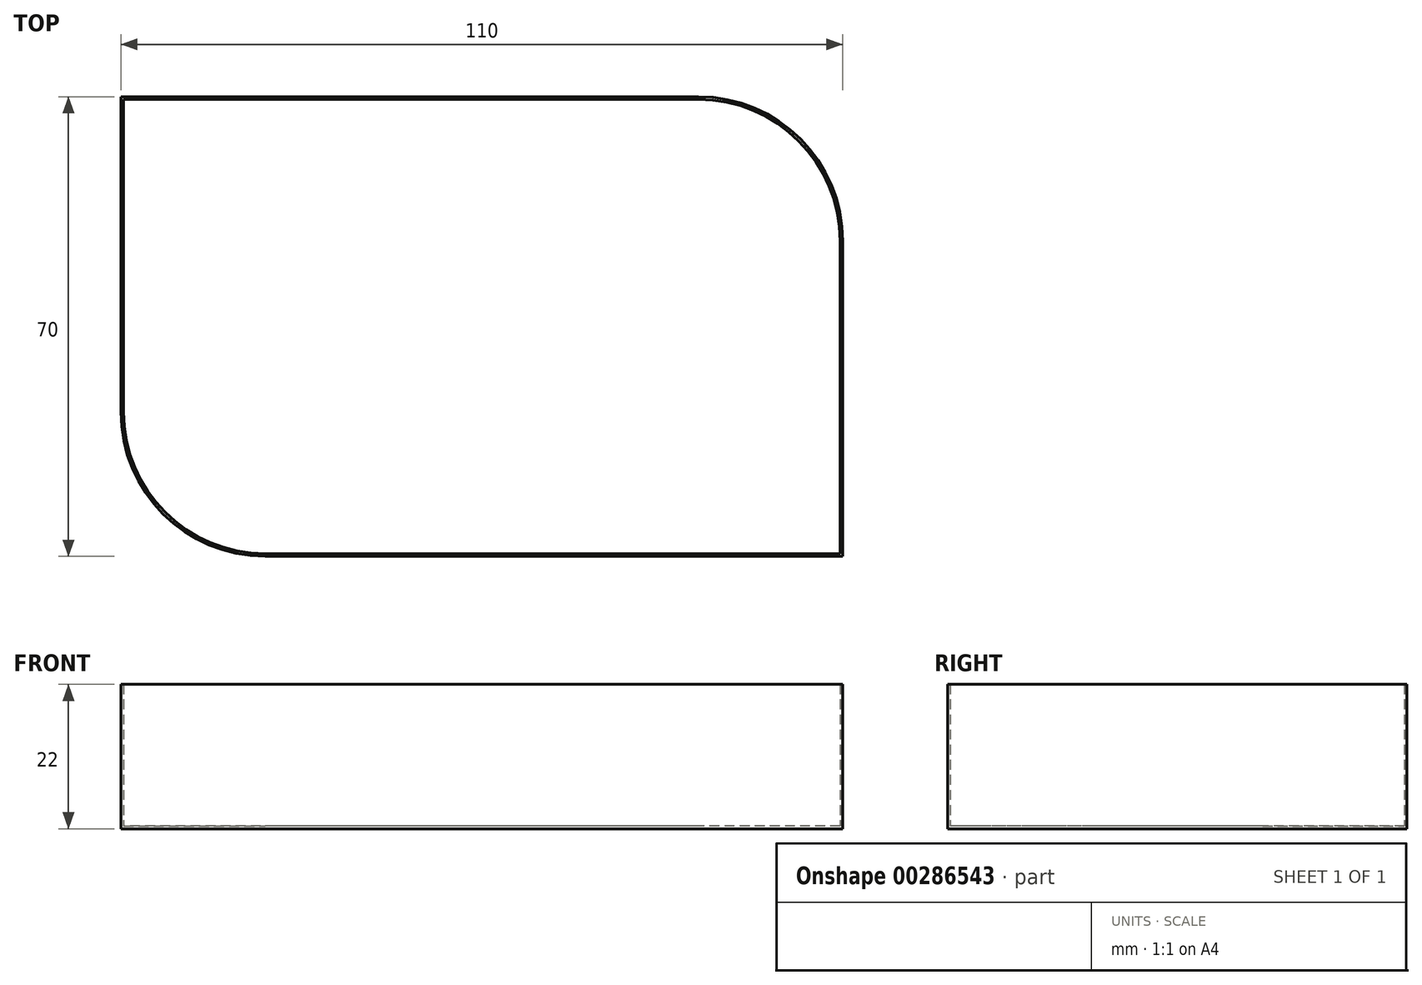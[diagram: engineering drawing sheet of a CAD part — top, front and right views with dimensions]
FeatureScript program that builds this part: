
annotation { "Feature Type Name" : "Feature", "Feature Type Description" : "" }
export const myFeature = defineFeature(function(context is Context, id is Id, definition is map)
    precondition{}
    {
        {
            var Q0;
            Q0=qCreatedBy(makeId("Top.planeOp"),FACE);
            var sketch = newSketch(context, id + "F0", { "sketchPlane" : qUnion([Q0])});
            skLineSegment(sketch, "E0.bottom", {"start": v(33, 35) * mm, "end": v(-55, 35) * mm});
            skLineSegment(sketch, "E0.top", {"start": v(55, -35) * mm, "end": v(-33, -35) * mm});
            skLineSegment(sketch, "E0.left", {"start": v(55, 13) * mm, "end": v(55, -35) * mm});
            skLineSegment(sketch, "E0.right", {"start": v(-55, 35) * mm, "end": v(-55, -13) * mm});
            skPoint(sketch, "E0.middle", {"position": v(0, 0) * mm});
            skPoint(sketch, "E1.visualSharp", {"position": v(55, 35) * mm});
            skArc(sketch, "E1.filletArc", {"start": v(55, 13) * mm, "mid": v(48.56, 28.56) * mm, "end": v(33, 35) * mm});
            skPoint(sketch, "E2.visualSharp", {"position": v(-55, -35) * mm});
            skArc(sketch, "E2.filletArc", {"start": v(-55, -13) * mm, "mid": v(-48.56, -28.56) * mm, "end": v(-33, -35) * mm});
            skSolve(sketch);
        }
        {
            var Q0;
            Q0 = qSketchRegion(id + "F0", true);
            extrude(context, id + "F1", {"entities" : qUnion([Q0]), "depth" : 22 * mm});
        }
        {
            var Q0;
            Q0=makeQuery(id+"F1.opExtrude","CAP_FACE",FACE,{"disambiguationData":[OSD([sQuery(id+"F0.wireOp",EDGE,"E0.bottom"),sQuery(id+"F0.wireOp",EDGE,"E0.top"),sQuery(id+"F0.wireOp",EDGE,"E0.left"),sQuery(id+"F0.wireOp",EDGE,"E0.right"),sQuery(id+"F0.wireOp",EDGE,"E1.filletArc"),sQuery(id+"F0.wireOp",EDGE,"E2.filletArc")])],"isStart":false});
            shell(context, id + "F2", {"entities" : qUnion([Q0]), "thickness" : 0.4 * mm});
        }
    });
